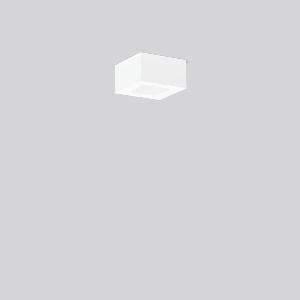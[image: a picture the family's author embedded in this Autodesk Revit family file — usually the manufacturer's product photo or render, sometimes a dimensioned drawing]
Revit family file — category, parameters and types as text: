
# Revit family: toledo_flat_square_a_672259_002_89_c50c
name_source: partatom
category: Lighting Fixtures
units: mm (PartAtom-declared; Revit-internal decimal feet)

## family parameters
Cut with Voids When Loaded = No
Host = Face
Light Source = No
Part Type = Normal
Room Calculation Point = No
Round Connector Dimension = Use Diameter
Shared = No

## types (1)
- TOLEDO FLAT square A (1 x LED Modul 830, 410 lm, 3000)
    Apparent Load = 7 VA
    CIE Flux Codes = 48 80 96 100 100
    Color Rendering = 80
    Color Temperature = 3000
    Default Elevation = 1800 mm
    Description = Series: TOLEDO FLAT square
Ultra thin surface mounted downlight. For escape route illumination. Surface mounted housing: sheet steel, powder-coated. Square cover plate: die-cast aluminium, powder coated. Light guide and diffuser made of non-yellowing PMMA, opal matt. Driver integrated. Suitable for connection to central battery systems. With AC Control monitoring module for LUXIFAIR central battery units. 
Colour: white
Length: 110 mm
Width: 110 mm
Height: 58 mm
Weight: 615 g
Operating mode: maintained power mode
Lamp: LED
Socket: without socket
Colour temperature: 3000K
Colour rendering index (CRI): 80
System power: 7 W
Rated luminous flux: 410 lm
Luminous flux, emergency: 410 lm
System power, emergency: 7 W
Control gear: Regulated power supply
Protection class: I
Type of protection: IP 40
    Height = 58 mm
    Lamp = 1 x LED Modul 830
    Lamp Light Flux = 410 lm
    Lamp count = 1
    Length = 110 mm
    Lifetime = 50000 h
    Luminous efficacy = 59 lm/W
    Manufacturer = RZB
    ModVariant = No
    Model = 672259.002.89
    Mounting Place = Ceiling
    Mounting Type = Surface mounted
    Number of Poles = 1
    OnlyDefault = Yes
    Power Factor = 1
    Product Name = TOLEDO FLAT square A
    Product group = Surface mounted downlights
    ProductGroupID = 302
    Protection Class = Protection class I
    Protection Degree = IP 40
    RLX_Detail_Level = 1
    RLX_Emergency_Light_Flux = 410 lm
    RLX_Emergency_Type = 3
    RLX_Emergency_Type_DB = Yes
    RlxData = <blob elided: 8689 chars, md5=62086327>
    Socket = socket
    Standby Power = 0 W
    System Light Flux = 410 lm
    System Power = 7 W
    Type Comments = Product without accessories
    Type Image = 901551.002.jpg
    URL = http://relux.com
    VarID = ---
    Voltage = 230 V
    Voltage Range = 220-240 V
    Weight = 0.00 kg
    Width = 110 mm

## geometry (parser evidence)
native form markers: Blend x4, Sweep x11
no freeform markers — native parametric forms only
